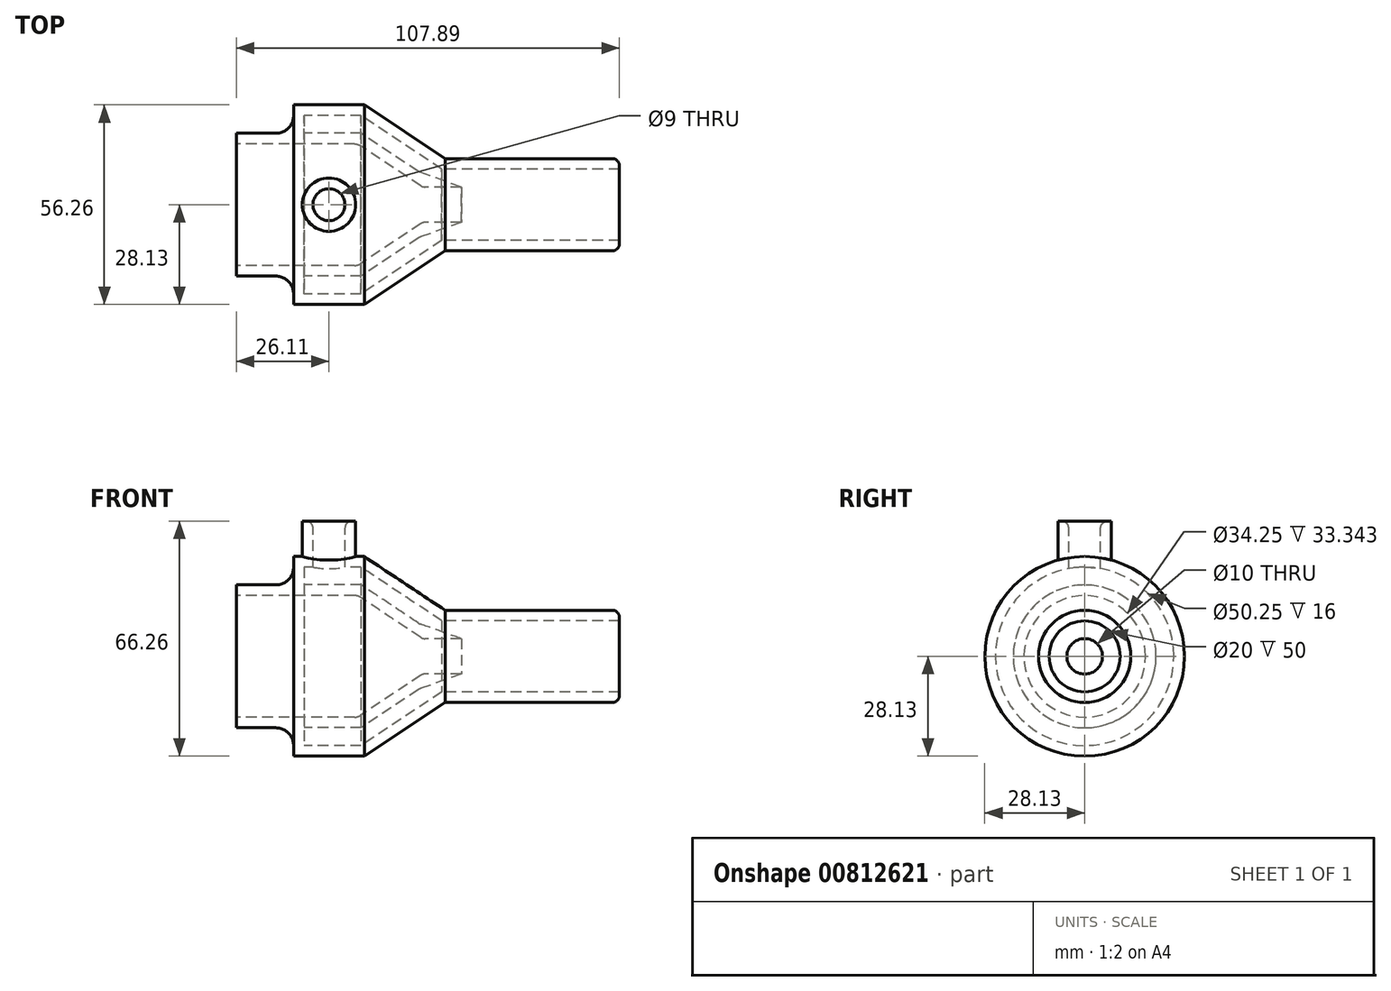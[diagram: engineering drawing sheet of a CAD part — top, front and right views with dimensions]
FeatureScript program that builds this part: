
annotation { "Feature Type Name" : "Feature", "Feature Type Description" : "" }
export const myFeature = defineFeature(function(context is Context, id is Id, definition is map)
    precondition{}
    {
        {
            var Q0;
            Q0=qCreatedBy(makeId("Front.planeOp"),FACE);
            var sketch = newSketch(context, id + "F0", { "sketchPlane" : qUnion([Q0])});
            skLineSegment(sketch, "E0", {"start": v(-57.89, 17.12) * mm, "end": v(-23.64, 17.12) * mm});
            skLineSegment(sketch, "E1", {"start": v(-23.64, 17.13) * mm, "end": v(-5.42, 5) * mm});
            skLineSegment(sketch, "E2.0", {"start": v(-22.73, 20.13) * mm, "end": v(-6.32, 9.2) * mm});
            skLineSegment(sketch, "E2.1", {"start": v(-57.89, 20.12) * mm, "end": v(-22.73, 20.12) * mm});
            skLineSegment(sketch, "E3", {"start": v(-6.32, 9.2) * mm, "end": v(-5.42, 5) * mm});
            skLineSegment(sketch, "E4", {"start": v(-57.89, 20.13) * mm, "end": v(-57.89, 17.13) * mm});
            skLineSegment(sketch, "E5", {"start": v(0, 10) * mm, "end": v(50, 10) * mm});
            skLineSegment(sketch, "E6", {"start": v(0, 10) * mm, "end": v(-22.73, 25.12) * mm});
            skLineSegment(sketch, "E7", {"start": v(-22.73, 25.12) * mm, "end": v(-38.73, 25.12) * mm});
            skLineSegment(sketch, "E8", {"start": v(-38.73, 25.12) * mm, "end": v(-38.73, 20.12) * mm});
            skPoint(sketch, "E8.endSnap0", {"position": v(-40.31, 20.13) * mm});
            skLineSegment(sketch, "E9.0", {"start": v(0.9, 13) * mm, "end": v(50, 13) * mm});
            skLineSegment(sketch, "E9.1", {"start": v(0.9, 13) * mm, "end": v(-21.83, 28.13) * mm});
            skLineSegment(sketch, "E9.2", {"start": v(-21.83, 28.12) * mm, "end": v(-41.73, 28.12) * mm});
            skLineSegment(sketch, "E9.3", {"start": v(-41.73, 28.12) * mm, "end": v(-41.73, 20.12) * mm});
            skLineSegment(sketch, "E10", {"start": v(50, 13) * mm, "end": v(50, 10) * mm});
            skLineSegment(sketch, "E11", {"start": v(-56.48, 0) * mm, "end": v(31.38, 0) * mm, "construction": true});
            skLineSegment(sketch, "E12", {"start": v(-5.42, 5) * mm, "end": v(5.47, 5) * mm});
            skLineSegment(sketch, "E13", {"start": v(-6.32, 9.2) * mm, "end": v(5.47, 5) * mm});
            skSolve(sketch);
        }
        {
            var Q0;
            Q0=qSketchRegion(id+"F0",true);
            var Q1;
            Q1=sQuery(id+"F0.wireOp",EDGE,"E11");
            revolve(context, id + "F1", {"surfaceOperationType" : NewSurfaceOperationType.NEW, "entities" : qUnion([Q0]), "axis" : qUnion([Q1]), "revolveType" : RevolveType.FULL});
        }
        {
            var Q0;
            Q0=qCreatedBy(makeId("Right.planeOp"),FACE);
            var sketch = newSketch(context, id + "F2", { "sketchPlane" : qUnion([Q0])});
            skCircle(sketch, "E14.0", {"center": v(0, 0) * mm, "radius": 28.12 * mm, "construction": true});
            skLineSegment(sketch, "E15", {"start": v(32.58, 28.12) * mm, "end": v(-33.03, 28.12) * mm, "construction": true});
            skSolve(sketch);
        }
        {
            var Q0;
            Q0=makeQuery(id+"F1.opRevolve","SWEPT_FACE",FACE,{"disambiguationData":[OSD([sQuery(id+"F0.wireOp",EDGE,"E9.3")])]});
            var sketch = newSketch(context, id + "F3", { "sketchPlane" : qUnion([Q0])});
            skLineSegment(sketch, "E16.0", {"start": v(-32.58, 28.12) * mm, "end": v(33.03, 28.12) * mm, "construction": true});
            skSolve(sketch);
        }
        {
            var Q0;
            Q0=sQuery(id+"F3.wireOp",VERTEX,"E16.0.start");
            var Q1;
            Q1=sQuery(id+"F2.wireOp",VERTEX,"E15.start");
            var Q2;
            Q2=sQuery(id+"F3.wireOp",VERTEX,"E16.0.end");
            cPlane(context, id + "F4", {"entities" : qUnion([Q0, Q1, Q2]), "cplaneType" : CPlaneType.THREE_POINT, "offset" : 25 * mm, "width" : 150 * mm, "height" : 150 * mm});
        }
        {
            var Q0;
            Q0=qCreatedBy(id+"F4.planeOp",FACE);
            var sketch = newSketch(context, id + "F5", { "sketchPlane" : qUnion([Q0])});
            skLineSegment(sketch, "E17.0", {"start": v(-41.73, 32.58) * mm, "end": v(-41.73, -33.03) * mm});
            skLineSegment(sketch, "E17.1", {"start": v(-21.83, -28.13) * mm, "end": v(-21.83, 28.13) * mm});
            skLineSegment(sketch, "E18", {"start": v(-21.83, 0) * mm, "end": v(-41.73, 0) * mm, "construction": true});
            skCircle(sketch, "E19", {"center": v(-31.78, 0) * mm, "radius": 4.5 * mm});
            skCircle(sketch, "E20.0", {"center": v(-31.78, 0) * mm, "radius": 7.5 * mm});
            skSolve(sketch);
        }
        {
            var Q0;
            Q0=makeQuery(id+"F5.imprint","IMPRINT",FACE,{"disambiguationData":[TD([[makeQuery(id+"F5.imprint","IMPRINT",EDGE,{"derivedFrom":sQuery(id+"F5.wireOp",EDGE,"E19")}),1.0]])]});
            var Q1;
            Q1=makeQuery(id+"F1.opRevolve","SWEPT_FACE",FACE,{"disambiguationData":[OSD([sQuery(id+"F0.wireOp",EDGE,"E7")])]});
            extrude(context, id + "F6", {"entities" : qUnion([Q0]), "operationType" : NewBodyOperationType.REMOVE, "endBound" : BoundingType.UP_TO_SURFACE, "oppositeDirection" : true, "depth" : 25 * mm, "endBoundEntityFace" : qUnion([Q1]), "offsetDistance" : 25 * mm});
        }
        {
            var Q0;
            Q0=qSketchRegion(id+"F5",true);
            var Q1;
            Q1=makeQuery(id+"F1.opRevolve","SWEPT_BODY",BODY,{"disambiguationData":[OSD([sQuery(id+"F0.wireOp",EDGE,"E0"),sQuery(id+"F0.wireOp",EDGE,"E1"),sQuery(id+"F0.wireOp",EDGE,"E2.0"),sQuery(id+"F0.wireOp",EDGE,"E2.1"),sQuery(id+"F0.wireOp",EDGE,"E4"),sQuery(id+"F0.wireOp",EDGE,"E5"),sQuery(id+"F0.wireOp",EDGE,"E6"),sQuery(id+"F0.wireOp",EDGE,"E7"),sQuery(id+"F0.wireOp",EDGE,"E8"),sQuery(id+"F0.wireOp",EDGE,"E9.0"),sQuery(id+"F0.wireOp",EDGE,"E9.1"),sQuery(id+"F0.wireOp",EDGE,"E9.2"),sQuery(id+"F0.wireOp",EDGE,"E9.3"),sQuery(id+"F0.wireOp",EDGE,"E10"),sQuery(id+"F0.wireOp",EDGE,"E12"),sQuery(id+"F0.wireOp",EDGE,"E13")])]});
            extrude(context, id + "F7", {"entities" : qUnion([Q0]), "operationType" : NewBodyOperationType.ADD, "depth" : 10 * mm, "offsetDistance" : 25 * mm, "hasSecondDirection" : true, "secondDirectionBound" : SecondDirectionBoundingType.UP_TO_BODY, "secondDirectionOppositeDirection" : true, "secondDirectionDepth" : 25 * mm, "secondDirectionBoundEntityBody" : qUnion([Q1])});
        }
        {
            var Q0;
            Q0=makeQuery(id+"F1.opRevolve","SWEPT_EDGE",EDGE,{"disambiguationData":[OSD([sQuery(id+"F0.wireOp",EDGE,"E2.1"),sQuery(id+"F0.wireOp",EDGE,"E9.3")])]});
            fillet(context, id + "F8", {"entities" : qUnion([Q0]), "radius" : 5 * mm, "tangentPropagation" : true, "allowEdgeOverflow" : false});
        }
        {
            var Q0;
            Q0=makeQuery(id+"F1.opRevolve","SWEPT_EDGE",EDGE,{"disambiguationData":[OSD([sQuery(id+"F0.wireOp",EDGE,"E2.0"),sQuery(id+"F0.wireOp",EDGE,"E3")])]});
            var Q1;
            Q1=makeQuery(id+"F1.opRevolve","SWEPT_EDGE",EDGE,{"disambiguationData":[OSD([sQuery(id+"F0.wireOp",EDGE,"E0"),sQuery(id+"F0.wireOp",EDGE,"E1")])]});
            fillet(context, id + "F9", {"entities" : qUnion([Q0, Q1]), "radius" : 3 * mm, "tangentPropagation" : true, "allowEdgeOverflow" : false});
        }
        {
            var Q0;
            Q0=makeQuery(id+"F7.opExtrude","CAP_EDGE",EDGE,{"disambiguationData":[OSD([sQuery(id+"F5.wireOp",EDGE,"E20.0")]),topologyDisambiguationEdgeConnected([makeQuery(id+"F1.opRevolve","SWEPT_FACE",FACE,{"disambiguationData":[OSD([sQuery(id+"F0.wireOp",EDGE,"E9.2")])]})])],"isStart":false});
            var Q1;
            Q1=makeQuery(id+"F7.opExtrude","CAP_EDGE",EDGE,{"disambiguationData":[OSD([sQuery(id+"F5.wireOp",EDGE,"E19")])],"isStart":false});
            fillet(context, id + "F10", {"entities" : qUnion([Q0, Q1]), "radius" : 2 * mm, "tangentPropagation" : true, "allowEdgeOverflow" : false});
        }
        {
            var Q0;
            Q0=makeQuery(id+"F1.opRevolve","SWEPT_EDGE",EDGE,{"disambiguationData":[OSD([sQuery(id+"F0.wireOp",EDGE,"E9.0"),sQuery(id+"F0.wireOp",EDGE,"E10")])]});
            var Q1;
            Q1=makeQuery(id+"F1.opRevolve","SWEPT_EDGE",EDGE,{"disambiguationData":[OSD([sQuery(id+"F0.wireOp",EDGE,"E1"),sQuery(id+"F0.wireOp",EDGE,"E3"),sQuery(id+"F0.wireOp",EDGE,"E12")])]});
            fillet(context, id + "F11", {"entities" : qUnion([Q0, Q1]), "radius" : 2 * mm, "tangentPropagation" : true, "allowEdgeOverflow" : false});
        }
    });
